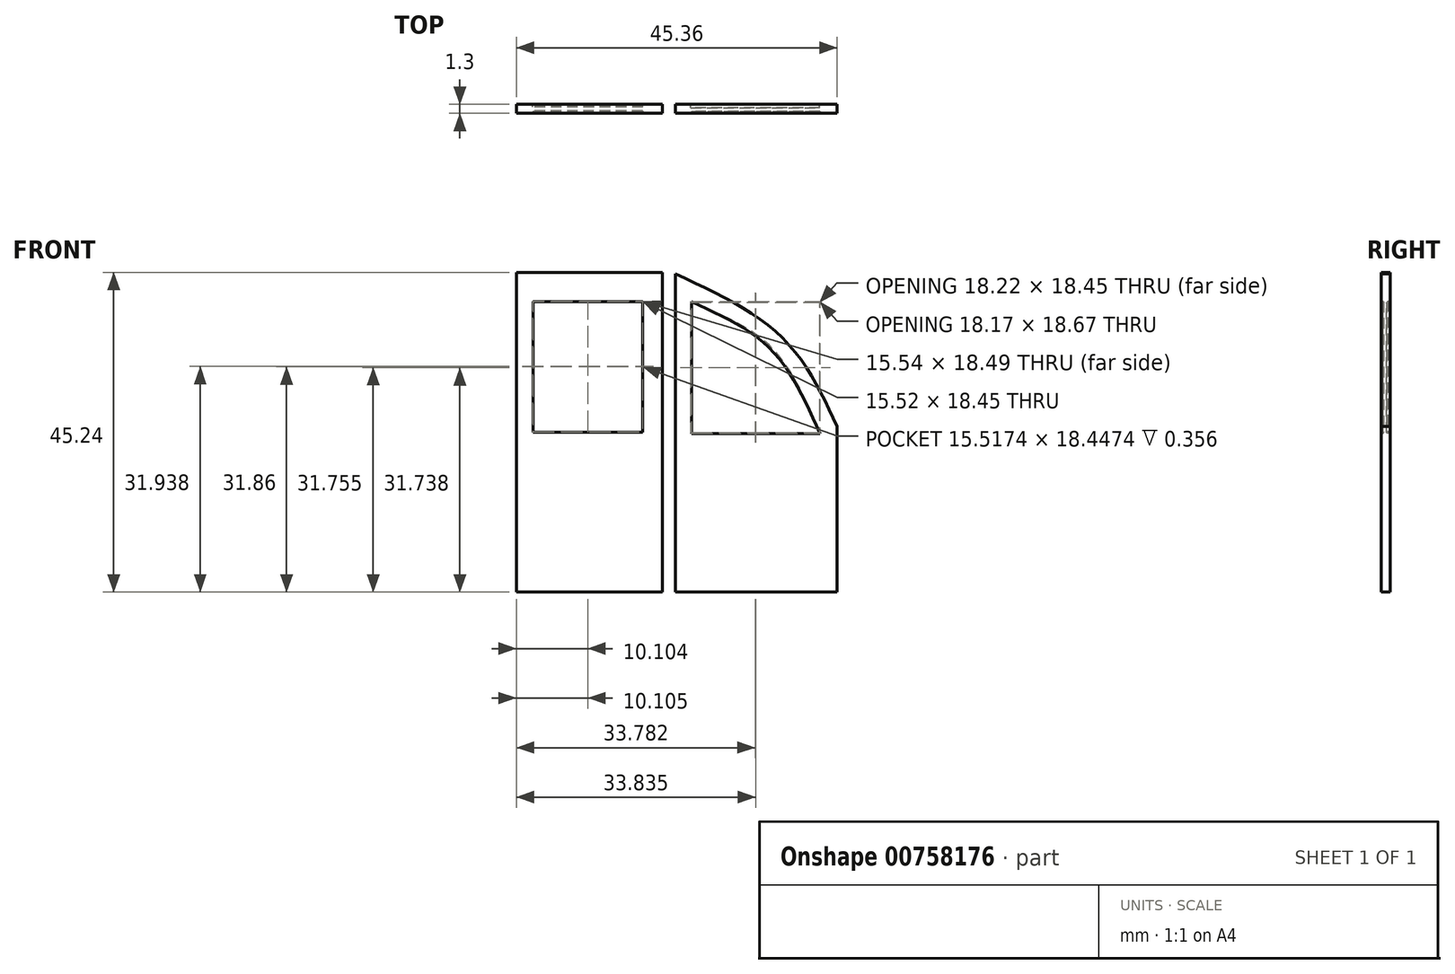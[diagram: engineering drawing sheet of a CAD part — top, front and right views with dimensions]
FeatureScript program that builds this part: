
annotation { "Feature Type Name" : "Feature", "Feature Type Description" : "" }
export const myFeature = defineFeature(function(context is Context, id is Id, definition is map)
    precondition{}
    {
        {
            var Q0;
            Q0=qCreatedBy(makeId("Front.planeOp"),FACE);
            var sketch = newSketch(context, id + "F0", { "sketchPlane" : qUnion([Q0])});
            skLineSegment(sketch, "E0.bottom", {"start": v(-15.3, 14.75) * mm, "end": v(-35.95, 14.75) * mm});
            skLineSegment(sketch, "E0.top", {"start": v(-15.3, 59.96) * mm, "end": v(-35.95, 59.96) * mm});
            skLineSegment(sketch, "E0.left", {"start": v(-15.3, 14.75) * mm, "end": v(-15.3, 59.96) * mm});
            skLineSegment(sketch, "E0.right", {"start": v(-35.95, 14.75) * mm, "end": v(-35.95, 59.96) * mm});
            skSolve(sketch);
        }
        {
            var Q0;
            Q0=makeQuery(id+"F0.imprint","IMPRINT",FACE,{"disambiguationData":[TD([[makeQuery(id+"F0.imprint","IMPRINT",EDGE,{"derivedFrom":sQuery(id+"F0.wireOp",EDGE,"E0.bottom")}),-1.0]])]});
            extrude(context, id + "F1", {"entities" : qUnion([Q0]), "depth" : 1.3 * mm, "offsetDistance" : 25.4 * mm});
        }
        {
            var Q0;
            Q0=makeQuery(id+"F1.opExtrude","CAP_FACE",FACE,{"disambiguationData":[OSD([sQuery(id+"F0.wireOp",EDGE,"E0.bottom"),sQuery(id+"F0.wireOp",EDGE,"E0.top"),sQuery(id+"F0.wireOp",EDGE,"E0.left"),sQuery(id+"F0.wireOp",EDGE,"E0.right")])],"isStart":false});
            var sketch = newSketch(context, id + "F2", { "sketchPlane" : qUnion([Q0])});
            skPoint(sketch, "E1.oppositeSnap0", {"position": v(-35.95, 37.36) * mm});
            skLineSegment(sketch, "E1.bottom", {"start": v(-18.09, 55.8) * mm, "end": v(-33.6, 55.8) * mm});
            skLineSegment(sketch, "E1.top", {"start": v(-18.09, 37.36) * mm, "end": v(-33.6, 37.36) * mm});
            skLineSegment(sketch, "E1.left", {"start": v(-18.09, 55.8) * mm, "end": v(-18.09, 37.36) * mm});
            skLineSegment(sketch, "E1.right", {"start": v(-33.6, 55.8) * mm, "end": v(-33.6, 37.36) * mm});
            skSolve(sketch);
        }
        {
            var Q0;
            Q0=makeQuery(id+"F2.imprint","IMPRINT",FACE,{"disambiguationData":[TD([[makeQuery(id+"F2.imprint","IMPRINT",EDGE,{"derivedFrom":sQuery(id+"F2.wireOp",EDGE,"E1.bottom")}),1.0]])]});
            extrude(context, id + "F3", {"entities" : qUnion([Q0]), "operationType" : NewBodyOperationType.REMOVE, "oppositeDirection" : true, "depth" : 0.36 * mm, "offsetDistance" : 25.4 * mm});
        }
        {
            var Q0;
            Q0=qCreatedBy(makeId("Front.planeOp"),FACE);
            var sketch = newSketch(context, id + "F4", { "sketchPlane" : qUnion([Q0])});
            skLineSegment(sketch, "E2", {"start": v(-13.45, 59.76) * mm, "end": v(-13.45, 14.72) * mm});
            skLineSegment(sketch, "E3", {"start": v(-13.45, 14.72) * mm, "end": v(9.41, 14.72) * mm});
            skLineSegment(sketch, "E4", {"start": v(9.41, 14.72) * mm, "end": v(9.41, 38.15) * mm});
            skFitSpline(sketch, "E5", {"points": [v(9.41, 38.15) * mm, v(1.74, 50.62) * mm, v(-13.45, 59.76) * mm], "startDerivative": vector(-13.05, 28.26) * mm, "endDerivative": vector(-32.36, 15.17) * mm});
            skSolve(sketch);
        }
        {
            var Q0;
            Q0=makeQuery(id+"F4.imprint","IMPRINT",FACE,{"disambiguationData":[TD([[makeQuery(id+"F4.imprint","IMPRINT",EDGE,{"derivedFrom":sQuery(id+"F4.wireOp",EDGE,"E2")}),1.0]])]});
            extrude(context, id + "F5", {"entities" : qUnion([Q0]), "depth" : 1.27 * mm, "offsetDistance" : 25.4 * mm});
        }
        {
            var Q0;
            Q0=makeQuery(id+"F5.opExtrude","CAP_FACE",FACE,{"disambiguationData":[OSD([sQuery(id+"F4.wireOp",EDGE,"E2"),sQuery(id+"F4.wireOp",EDGE,"E3"),sQuery(id+"F4.wireOp",EDGE,"E4"),sQuery(id+"F4.wireOp",EDGE,"E5")])],"isStart":false});
            var sketch = newSketch(context, id + "F6", { "sketchPlane" : qUnion([Q0])});
            skLineSegment(sketch, "E6", {"start": v(-11.2, 55.8) * mm, "end": v(-11.2, 37.12) * mm});
            skLineSegment(sketch, "E7", {"start": v(-11.2, 37.12) * mm, "end": v(6.97, 37.12) * mm});
            skFitSpline(sketch, "E8", {"points": [v(6.97, 37.12) * mm, v(0, 49.09) * mm, v(-11.2, 55.8) * mm], "startDerivative": vector(-11.45, 26.11) * mm, "endDerivative": vector(-24.95, 11.15) * mm});
            skSolve(sketch);
        }
        {
            var Q0;
            Q0=makeQuery(id+"F6.imprint","IMPRINT",FACE,{"disambiguationData":[TD([[makeQuery(id+"F6.imprint","IMPRINT",EDGE,{"derivedFrom":sQuery(id+"F6.wireOp",EDGE,"E6")}),1.0]])]});
            extrude(context, id + "F7", {"entities" : qUnion([Q0]), "operationType" : NewBodyOperationType.REMOVE, "oppositeDirection" : true, "depth" : 0.25 * mm, "offsetDistance" : 25.4 * mm});
        }
        {
            var Q0;
            Q0=makeQuery(id+"F1.opExtrude","CAP_FACE",FACE,{"disambiguationData":[OSD([sQuery(id+"F0.wireOp",EDGE,"E0.bottom"),sQuery(id+"F0.wireOp",EDGE,"E0.top"),sQuery(id+"F0.wireOp",EDGE,"E0.left"),sQuery(id+"F0.wireOp",EDGE,"E0.right")])],"isStart":true});
            var sketch = newSketch(context, id + "F8", { "sketchPlane" : qUnion([Q0])});
            skLineSegment(sketch, "E9.bottom", {"start": v(18.07, 55.9) * mm, "end": v(33.62, 55.9) * mm});
            skLineSegment(sketch, "E9.top", {"start": v(18.07, 37.41) * mm, "end": v(33.62, 37.41) * mm});
            skLineSegment(sketch, "E9.left", {"start": v(18.07, 55.9) * mm, "end": v(18.07, 37.41) * mm});
            skLineSegment(sketch, "E9.right", {"start": v(33.62, 55.9) * mm, "end": v(33.62, 37.41) * mm});
            skSolve(sketch);
        }
        {
            var Q0;
            Q0 = qSketchRegion(id + "F8", true);
            extrude(context, id + "F9", {"entities" : qUnion([Q0]), "operationType" : NewBodyOperationType.REMOVE, "oppositeDirection" : true, "depth" : 0.38 * mm, "offsetDistance" : 25.4 * mm});
        }
        {
            var Q0;
            Q0=makeQuery(id+"F5.opExtrude","CAP_FACE",FACE,{"disambiguationData":[OSD([sQuery(id+"F4.wireOp",EDGE,"E2"),sQuery(id+"F4.wireOp",EDGE,"E3"),sQuery(id+"F4.wireOp",EDGE,"E4"),sQuery(id+"F4.wireOp",EDGE,"E5")])],"isStart":true});
            var sketch = newSketch(context, id + "F10", { "sketchPlane" : qUnion([Q0])});
            skLineSegment(sketch, "E10", {"start": v(11.28, 55.7) * mm, "end": v(11.28, 37.25) * mm});
            skLineSegment(sketch, "E11", {"start": v(11.28, 37.25) * mm, "end": v(-6.94, 37.25) * mm});
            skFitSpline(sketch, "E12", {"points": [v(-6.94, 37.25) * mm, v(0, 49.44) * mm, v(11.28, 55.7) * mm], "startDerivative": vector(11.2, 26.7) * mm, "endDerivative": vector(25.35, 10.08) * mm});
            skSolve(sketch);
        }
        {
            var Q0;
            Q0=makeQuery(id+"F10.imprint","IMPRINT",FACE,{"disambiguationData":[TD([[makeQuery(id+"F10.imprint","IMPRINT",EDGE,{"derivedFrom":sQuery(id+"F10.wireOp",EDGE,"E10")}),-1.0]])]});
            extrude(context, id + "F11", {"entities" : qUnion([Q0]), "operationType" : NewBodyOperationType.REMOVE, "oppositeDirection" : true, "depth" : 0.5 * mm, "offsetDistance" : 25.4 * mm});
        }
    });
